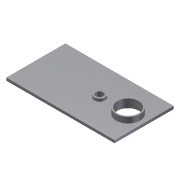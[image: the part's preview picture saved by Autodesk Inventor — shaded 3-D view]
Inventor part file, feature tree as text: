
AUTODESK INVENTOR PART (.ipt)
format: ipt  version: 2012 (Build 160160000, 160)  size: 98,304 bytes
history: native  units: mm
features: extrude x3, sketch x3
ambient origin geometry x8: Origin, YZ Plane, XZ Plane, XY Plane, X Axis, Y Axis, Z Axis, Center Point
bodies: Solid1 (feature_tree)
feature tree (6):
  extrude  "Extrusion1"  Depth=66.2mm
  extrude  "Extrusion2"  Depth=8.0mm
  extrude  "Extrusion3"  Depth=18.0mm
  sketch  "Sketch1"  dims[d0=121.2mm d1=66.2mm]
  sketch  "Sketch2"  dims[d3=33.1mm d4=8.0mm]
  sketch  "Sketch3"  dims[d5=23.8mm d6=18.0mm d8=3.0mm d9=0.0mm d10=12.0mm d11=3.0mm d12=0.0mm d13=23.8mm d14=26.8mm d15=6.4mm d16=0.0mm d17=31.8mm]
